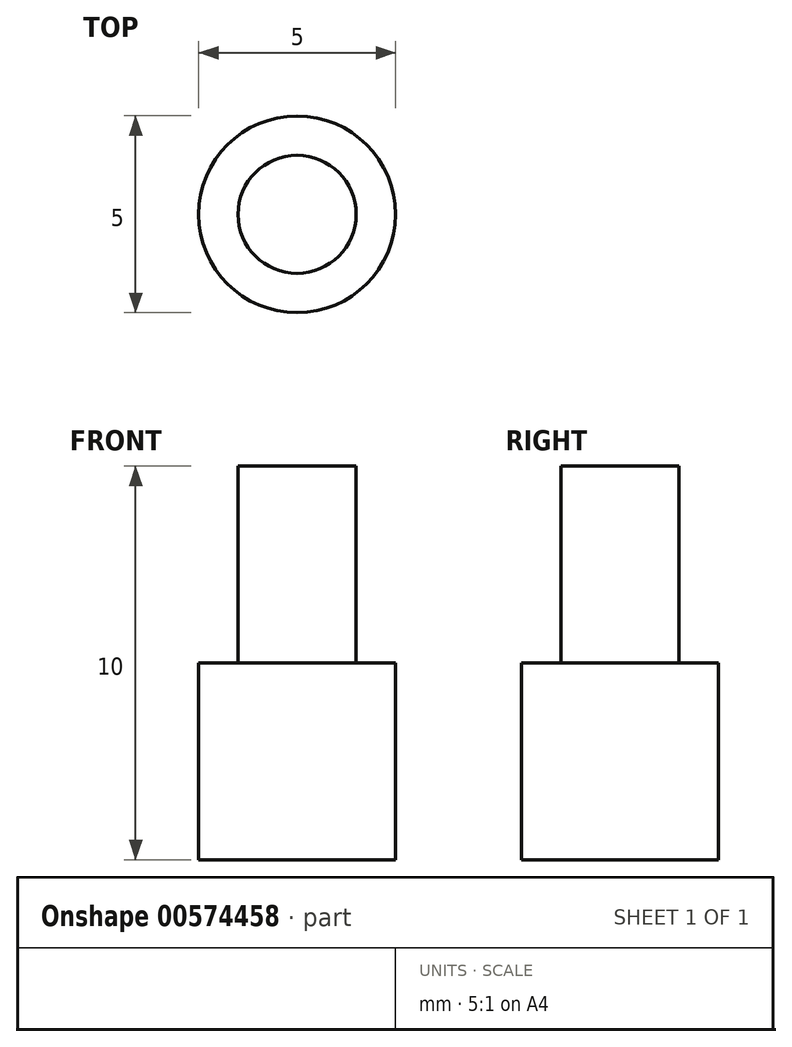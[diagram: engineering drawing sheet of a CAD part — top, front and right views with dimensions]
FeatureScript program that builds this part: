
annotation { "Feature Type Name" : "Feature", "Feature Type Description" : "" }
export const myFeature = defineFeature(function(context is Context, id is Id, definition is map)
    precondition{}
    {
        {
            var Q0;
            Q0=qCreatedBy(makeId("Top.planeOp"),FACE);
            var sketch = newSketch(context, id + "F0", { "sketchPlane" : qUnion([Q0])});
            skCircle(sketch, "E0", {"center": v(-39.5, 19.49) * mm, "radius": 2.5 * mm});
            skSolve(sketch);
        }
        {
            var Q0;
            Q0 = qSketchRegion(id + "F0", true);
            extrude(context, id + "F1", {"entities" : qUnion([Q0]), "depth" : 5 * mm, "offsetDistance" : 25 * mm});
        }
        {
            var Q0;
            Q0=makeQuery(id+"F1.opExtrude","CAP_FACE",FACE,{"disambiguationData":[OSD([sQuery(id+"F0.wireOp",EDGE,"E0")])],"isStart":false});
            var sketch = newSketch(context, id + "F2", { "sketchPlane" : qUnion([Q0])});
            skCircle(sketch, "E1", {"center": v(-39.5, 19.49) * mm, "radius": 1.5 * mm});
            skSolve(sketch);
        }
        {
            var Q0;
            Q0=makeQuery(id+"F2.imprint","IMPRINT",FACE,{"disambiguationData":[TD([[makeQuery(id+"F2.imprint","IMPRINT",EDGE,{"derivedFrom":sQuery(id+"F2.wireOp",EDGE,"E1")}),1.0]])]});
            extrude(context, id + "F3", {"entities" : qUnion([Q0]), "operationType" : NewBodyOperationType.ADD, "depth" : 5 * mm, "offsetDistance" : 25 * mm});
        }
    });
